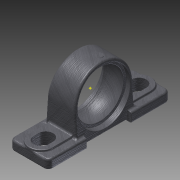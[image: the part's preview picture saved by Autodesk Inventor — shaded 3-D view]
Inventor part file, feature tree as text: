
AUTODESK INVENTOR PART (.ipt)
format: ipt  version: 2012 (Build 160160000, 160)  size: 690,688 bytes
history: native  units: mm
features: fillet x9, sketch x8, extrude x6, revolve x3, mirror x1, plane x1, projected_geometry x1
ambient origin geometry x8: Origin, YZ Plane, XZ Plane, XY Plane, X Axis, Y Axis, Z Axis, Center Point
bodies: Solid1 (feature_tree)
feature tree (29):
  sketch  "Sketch1"  dims[d0=60.0mm d2=3.0mm]
  revolve  "Revolution1"  [1 undecoded]
  sketch  "Sketch2"  dims[d3=4.0mm d4=3.0mm]
  revolve  "Revolution2"  [1 undecoded]
  extrude  "Extrusion2"  Depth=3.0mm
  extrude  "Extrusion3"  Depth=12.5mm
  extrude  "Extrusion4"  Depth=2.0mm
  extrude  "Extrusion5"  Depth=33.0mm TaperAngle=0.0deg
  extrude  "Extrusion6"  Depth=40.0mm
  mirror  "Mirror1"
  fillet  "Fillet1"  Radius=3.0mm
  fillet  "Fillet2"  Radius=40.0mm
  fillet  "Fillet3"  Radius=40.0mm
  fillet  "Fillet4"  Radius=12.5mm
  fillet  "Fillet5"  Radius=12.5mm
  fillet  "Fillet6"  Radius=12.5mm
  fillet  "Fillet7"  Radius=5.0mm
  fillet  "Fillet8"  Radius=5.0mm
  fillet  "Fillet9"  Radius=5.0mm
  plane  "Work Plane1"
  extrude  "Extrusion7"  Depth=12.5mm
  revolve  "Revolution3"  [1 undecoded]
  sketch  "Sketch3"  dims[d5=6.0mm d6=3.0mm]
  sketch  "Sketch4"  dims[d7=90.0deg d8=12.5mm]
  sketch  "Sketch5"  dims[d9=12.5mm d12=2.0mm]
  sketch  "Sketch6"  dims[d13=90.0deg d14=33.0mm d15=0.0mm]
  sketch  "Sketch7"  dims[d16=33.0mm d17=0.0mm d18=40.0mm d20=3.0mm d22=40.0mm d23=40.0mm d24=0.0mm d25=12.5mm d26=12.5mm d27=12.5mm d28=5.0mm d29=5.0mm d30=5.0mm]
  projected_geometry  "Projected Loop1"
  sketch  "Sketch8"  dims[d31=2.0mm d32=0.0mm d35=12.5mm d37=5.0mm d38=5.0mm d39=2.0mm d40=0.0mm d41=5.0mm d42=2.0mm d43=0.8mm d44=2.0mm d45=0.5mm d46=2.0mm d47=0.5mm d48=0.5mm d49=2.0mm d50=7.0mm d51=5.0mm d52=0.0mm d53=20.5mm d54=20.0mm d55=90.0deg]
note: 3 required parameter values undecoded (feature->parameter linkage not recoverable at this tier; creation-order binding heuristic only, values carry confidence <= 0.55)
